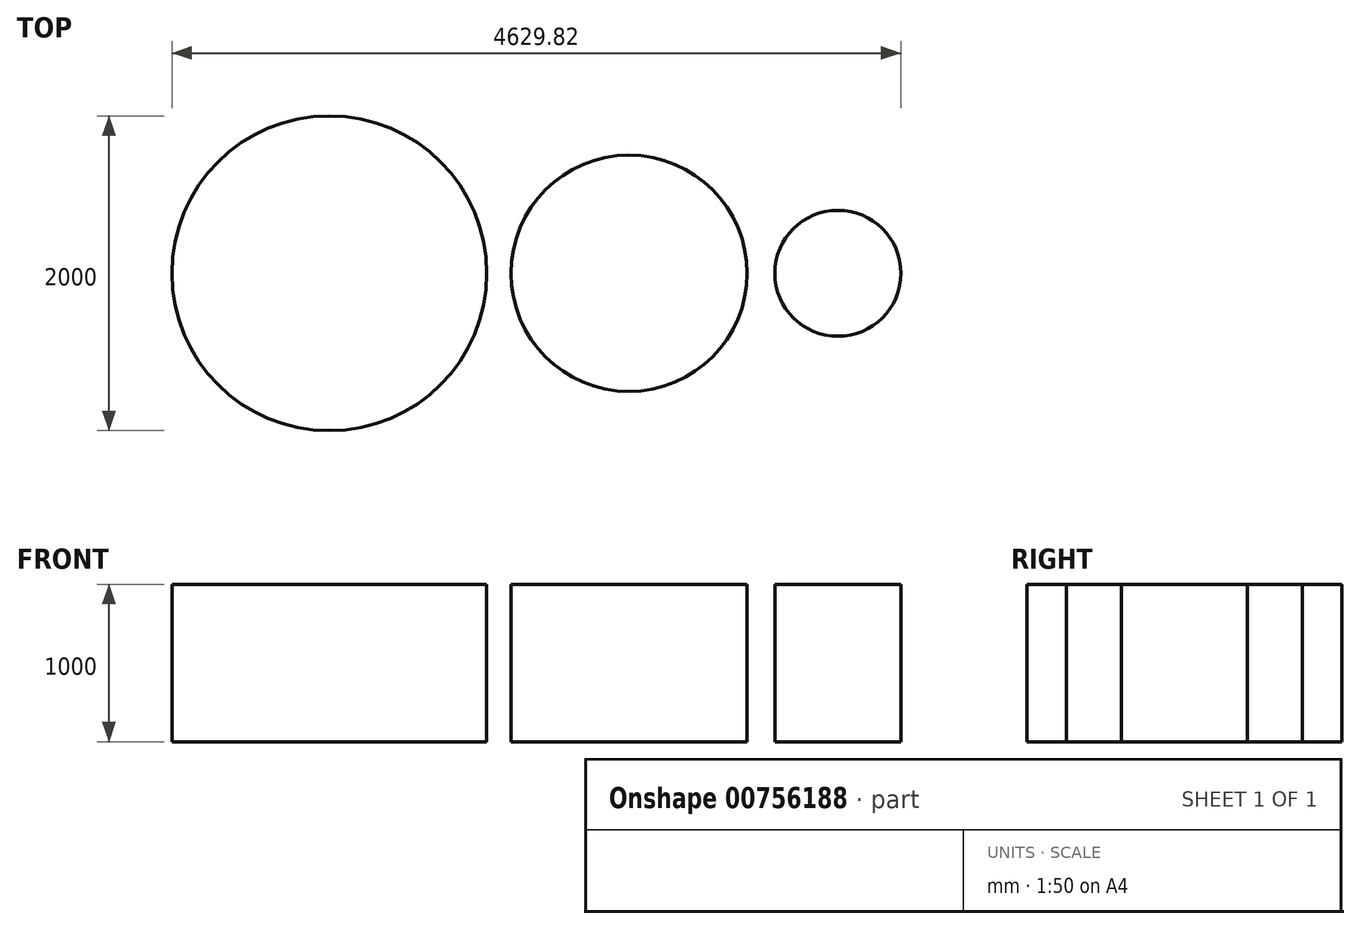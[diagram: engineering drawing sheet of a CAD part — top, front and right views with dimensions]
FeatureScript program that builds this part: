
annotation { "Feature Type Name" : "Feature", "Feature Type Description" : "" }
export const myFeature = defineFeature(function(context is Context, id is Id, definition is map)
    precondition{}
    {
        {
            var Q0;
            Q0=qCreatedBy(makeId("Top.planeOp"),FACE);
            var sketch = newSketch(context, id + "F0", { "sketchPlane" : qUnion([Q0])});
            skCircle(sketch, "E0", {"center": v(0, 0) * mm, "radius": 750 * mm});
            skCircle(sketch, "E1", {"center": v(1326.2, 0) * mm, "radius": 400 * mm});
            skCircle(sketch, "E2", {"center": v(-1903.63, 0) * mm, "radius": 1000 * mm});
            skSolve(sketch);
        }
        {
            var Q0;
            Q0=makeQuery(id+"F0.imprint","IMPRINT",FACE,{"disambiguationData":[TD([[makeQuery(id+"F0.imprint","IMPRINT",EDGE,{"derivedFrom":sQuery(id+"F0.wireOp",EDGE,"E2")}),1.0]])]});
            var Q1;
            Q1=makeQuery(id+"F0.imprint","IMPRINT",FACE,{"disambiguationData":[TD([[makeQuery(id+"F0.imprint","IMPRINT",EDGE,{"derivedFrom":sQuery(id+"F0.wireOp",EDGE,"E0")}),1.0]])]});
            var Q2;
            Q2=makeQuery(id+"F0.imprint","IMPRINT",FACE,{"disambiguationData":[TD([[makeQuery(id+"F0.imprint","IMPRINT",EDGE,{"derivedFrom":sQuery(id+"F0.wireOp",EDGE,"E1")}),1.0]])]});
            extrude(context, id + "F1", {"entities" : qUnion([Q0, Q1, Q2]), "depth" : 1000 * mm, "offsetDistance" : 25 * mm});
        }
    });
